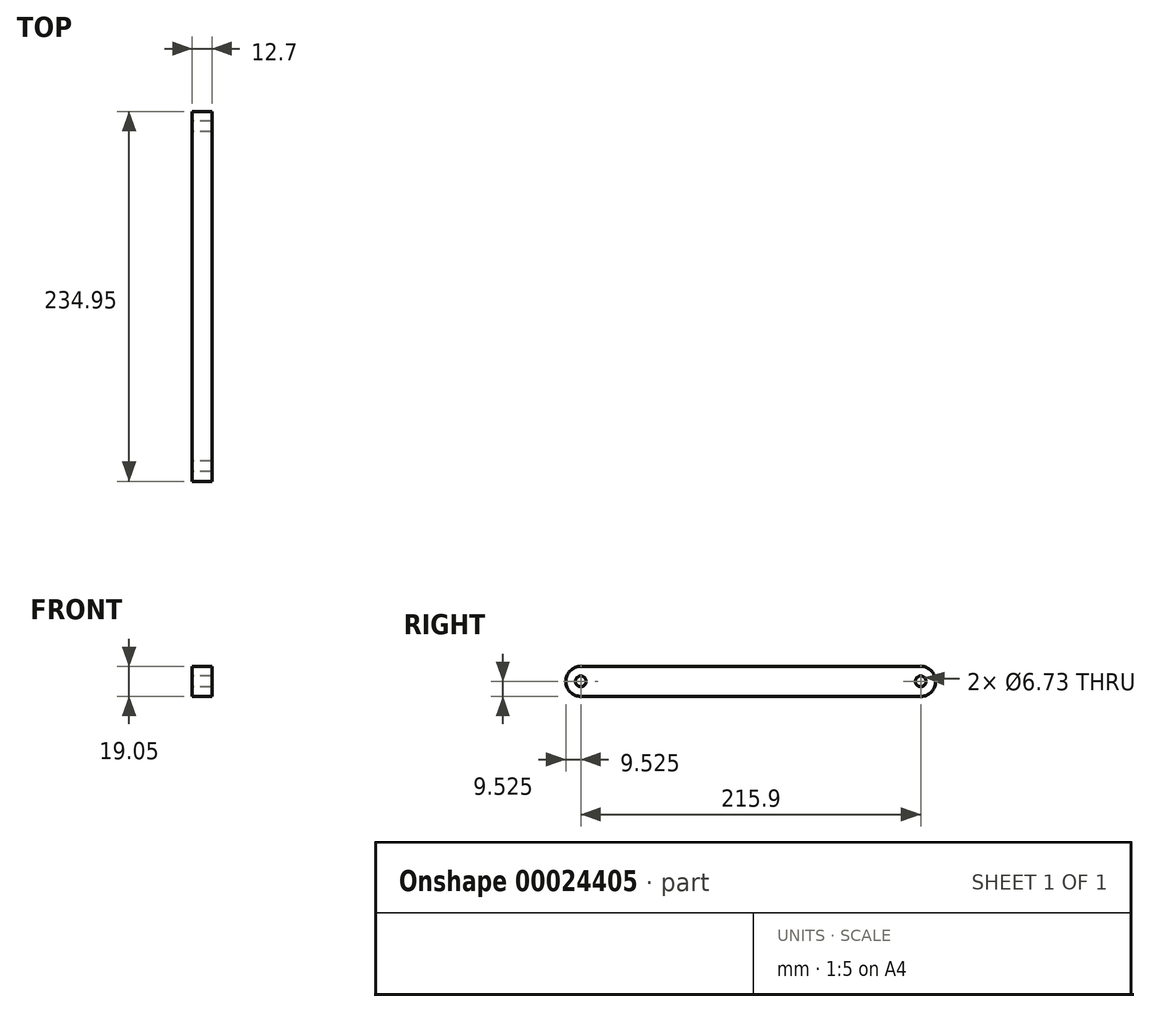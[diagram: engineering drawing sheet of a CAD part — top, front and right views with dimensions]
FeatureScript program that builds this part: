
annotation { "Feature Type Name" : "Feature", "Feature Type Description" : "" }
export const myFeature = defineFeature(function(context is Context, id is Id, definition is map)
    precondition{}
    {
        {
            var Q0;
            Q0=qCreatedBy(makeId("Right.planeOp"),FACE);
            var sketch = newSketch(context, id + "F0", { "sketchPlane" : qUnion([Q0])});
            skLineSegment(sketch, "E0.bottom", {"start": v(9.53, 0) * mm, "end": v(225.43, 0) * mm});
            skLineSegment(sketch, "E0.top", {"start": v(9.53, 19.05) * mm, "end": v(225.43, 19.05) * mm});
            skLineSegment(sketch, "E0.left", {"start": v(0, 9.52) * mm, "end": v(0, 9.52) * mm});
            skLineSegment(sketch, "E0.right", {"start": v(234.95, 9.53) * mm, "end": v(234.95, 9.53) * mm});
            skPoint(sketch, "E1.visualSharp", {"position": v(234.95, 19.05) * mm});
            skArc(sketch, "E1.filletArc", {"start": v(234.95, 9.53) * mm, "mid": v(232.16, 16.26) * mm, "end": v(225.43, 19.05) * mm});
            skPoint(sketch, "E2.visualSharp", {"position": v(234.95, 0) * mm});
            skArc(sketch, "E2.filletArc", {"start": v(225.43, 0) * mm, "mid": v(232.16, 2.79) * mm, "end": v(234.95, 9.53) * mm});
            skPoint(sketch, "E3.visualSharp", {"position": v(0, 0) * mm});
            skArc(sketch, "E3.filletArc", {"start": v(0, 9.52) * mm, "mid": v(2.79, 2.79) * mm, "end": v(9.53, 0) * mm});
            skPoint(sketch, "E4.visualSharp", {"position": v(0, 19.05) * mm});
            skArc(sketch, "E4.filletArc", {"start": v(9.52, 19.05) * mm, "mid": v(2.79, 16.26) * mm, "end": v(0, 9.52) * mm});
            skCircle(sketch, "E5", {"center": v(225.43, 9.53) * mm, "radius": 3.37 * mm});
            skCircle(sketch, "E6", {"center": v(9.53, 9.53) * mm, "radius": 3.37 * mm});
            skSolve(sketch);
        }
        {
            var Q0;
            Q0=makeQuery(id+"F0.imprint","IMPRINT",FACE,{"disambiguationData":[TD([[makeQuery(id+"F0.imprint","IMPRINT",EDGE,{"derivedFrom":sQuery(id+"F0.wireOp",EDGE,"E0.bottom")}),1.0]])]});
            extrude(context, id + "F1", {"entities" : qUnion([Q0]), "depth" : 12.7 * mm});
        }
    });
